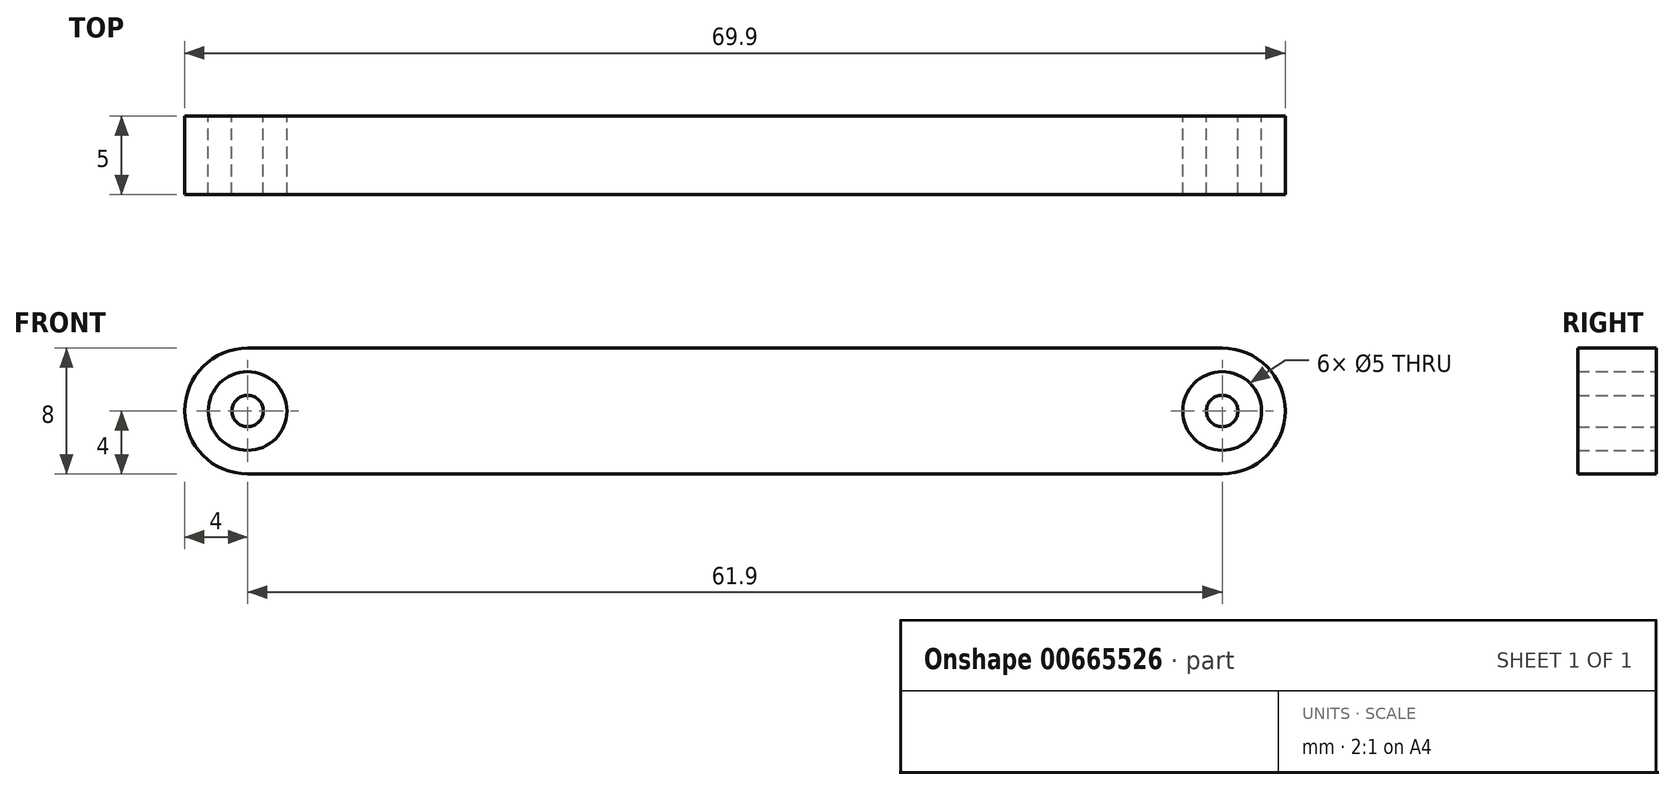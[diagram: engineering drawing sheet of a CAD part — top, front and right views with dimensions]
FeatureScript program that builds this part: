
annotation { "Feature Type Name" : "Feature", "Feature Type Description" : "" }
export const myFeature = defineFeature(function(context is Context, id is Id, definition is map)
    precondition{}
    {
        {
            var Q0;
            Q0=qCreatedBy(makeId("Front.planeOp"),FACE);
            var sketch = newSketch(context, id + "F0", { "sketchPlane" : qUnion([Q0])});
            skArc(sketch, "E0", {"start": v(0, 4) * mm, "mid": v(-4, 0) * mm, "end": v(0, -4) * mm});
            skArc(sketch, "E1", {"start": v(61.9, -4) * mm, "mid": v(65.9, 0) * mm, "end": v(61.9, 4) * mm});
            skLineSegment(sketch, "E2", {"start": v(0, 4) * mm, "end": v(61.9, 4) * mm});
            skLineSegment(sketch, "E3", {"start": v(0, -4) * mm, "end": v(61.9, -4) * mm});
            skCircle(sketch, "E4", {"center": v(0, 0) * mm, "radius": 2.5 * mm});
            skCircle(sketch, "E5", {"center": v(61.9, 0) * mm, "radius": 2.5 * mm});
            skCircle(sketch, "E6", {"center": v(0, 0) * mm, "radius": 1 * mm});
            skCircle(sketch, "E7", {"center": v(61.9, 0) * mm, "radius": 1 * mm});
            skSolve(sketch);
        }
        {
            var Q0;
            Q0 = qSketchRegion(id + "F0", true);
            var Q1;
            Q1=makeQuery(id+"F0.imprint","IMPRINT",FACE,{"disambiguationData":[TD([[makeQuery(id+"F0.imprint","IMPRINT",EDGE,{"derivedFrom":sQuery(id+"F0.wireOp",EDGE,"E6")}),1.0]])]});
            var Q2;
            Q2=makeQuery(id+"F0.imprint","IMPRINT",FACE,{"disambiguationData":[TD([[makeQuery(id+"F0.imprint","IMPRINT",EDGE,{"derivedFrom":sQuery(id+"F0.wireOp",EDGE,"E7")}),1.0]])]});
            extrude(context, id + "F1", {"entities" : qUnion([Q0, Q1, Q2]), "depth" : 5 * mm, "offsetDistance" : 25.4 * mm});
        }
    });
